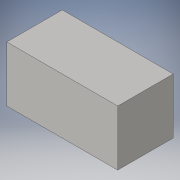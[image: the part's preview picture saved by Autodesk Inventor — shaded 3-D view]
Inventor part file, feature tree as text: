
AUTODESK INVENTOR PART (.ipt)
format: ipt  version: 2016 (Build 200138000, 138)  size: 79,872 bytes
history: native  units: in
note: dims shown in document units (in); Inventor stores cm internally (conversion verified against a paired STEP export)
features: extrude x1, sketch x1
ambient origin geometry x8: Origin, YZ Plane, XZ Plane, XY Plane, X Axis, Y Axis, Z Axis, Center Point
bodies: Solid1 (feature_tree)
feature tree (2):
  extrude  "Extrusion1"  Depth=1.0in
  sketch  "Sketch1"  dims[d0=2.0in d1=1.0in d2=1.0in d3=0.0in]
